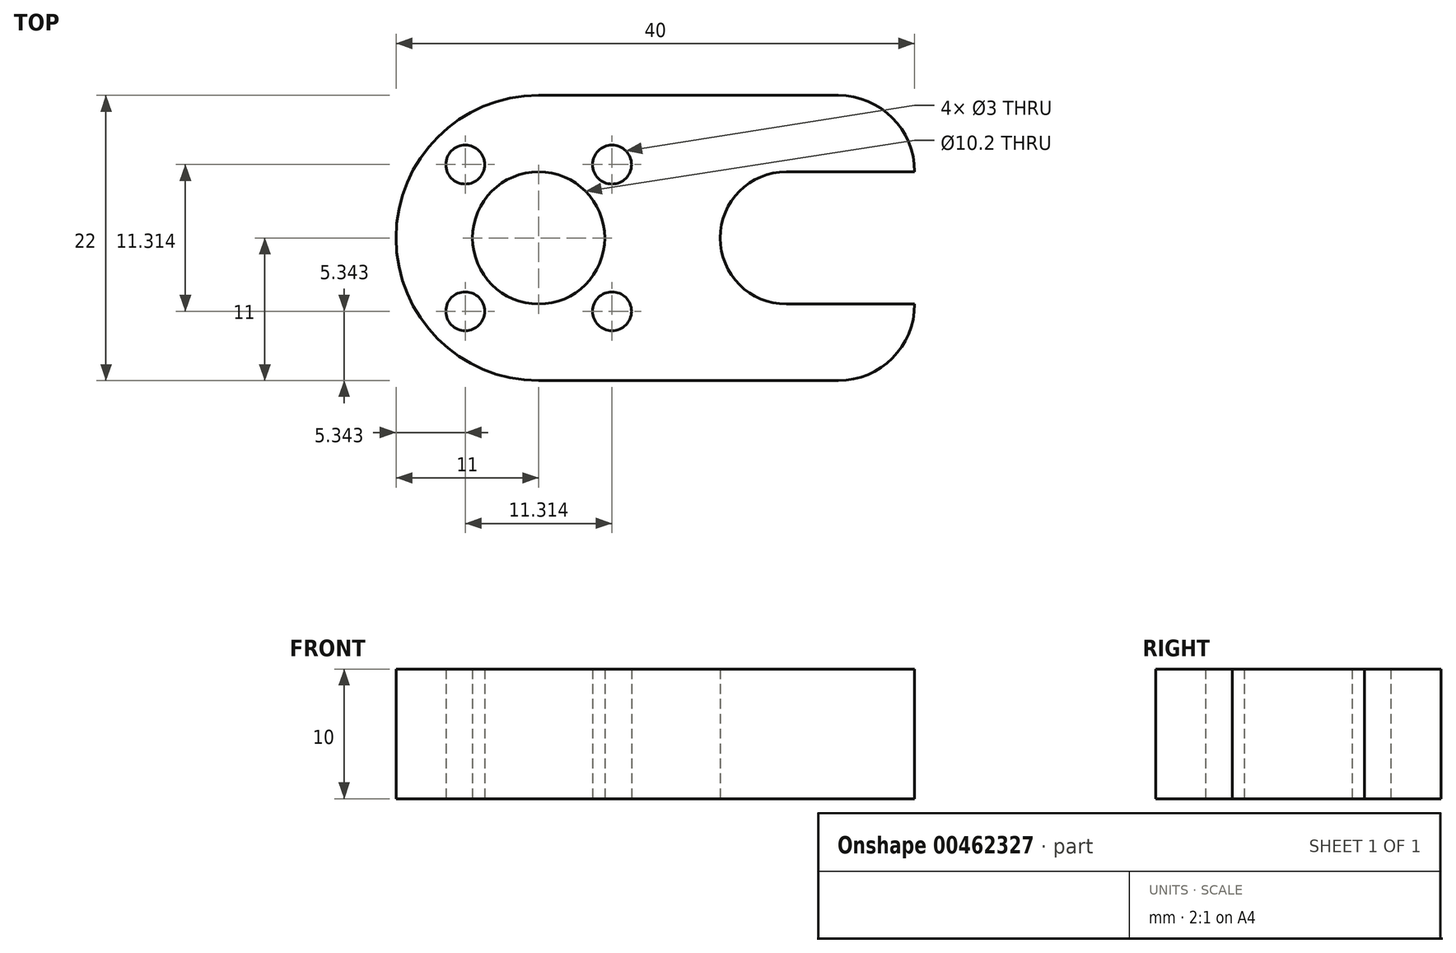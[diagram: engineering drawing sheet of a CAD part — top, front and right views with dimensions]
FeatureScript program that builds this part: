
annotation { "Feature Type Name" : "Feature", "Feature Type Description" : "" }
export const myFeature = defineFeature(function(context is Context, id is Id, definition is map)
    precondition{}
    {
        {
            var Q0;
            Q0=qCreatedBy(makeId("Top.planeOp"),FACE);
            var sketch = newSketch(context, id + "F0", { "sketchPlane" : qUnion([Q0])});
            skLineSegment(sketch, "E0.bottom", {"start": v(14.1, 11) * mm, "end": v(-9, 11) * mm});
            skLineSegment(sketch, "E0.top", {"start": v(14.1, -11) * mm, "end": v(-9, -11) * mm});
            skLineSegment(sketch, "E0.right", {"start": v(-20, 0) * mm, "end": v(-20, 0) * mm});
            skPoint(sketch, "E0.middle", {"position": v(0, 0) * mm});
            skPoint(sketch, "E1.visualSharp", {"position": v(-20, 11) * mm});
            skArc(sketch, "E1.filletArc", {"start": v(-9, 11) * mm, "mid": v(-16.78, 7.78) * mm, "end": v(-20, 0) * mm});
            skPoint(sketch, "E2.visualSharp", {"position": v(-20, -11) * mm});
            skArc(sketch, "E2.filletArc", {"start": v(-20, 0) * mm, "mid": v(-16.78, -7.78) * mm, "end": v(-9, -11) * mm});
            skPoint(sketch, "E3.visualSharp", {"position": v(20, 11) * mm});
            skArc(sketch, "E3.filletArc", {"start": v(20, 5.1) * mm, "mid": v(18.27, 9.27) * mm, "end": v(14.1, 11) * mm});
            skPoint(sketch, "E4.visualSharp", {"position": v(20, -11) * mm});
            skArc(sketch, "E4.filletArc", {"start": v(14.1, -11) * mm, "mid": v(18.27, -9.27) * mm, "end": v(20, -5.1) * mm});
            skLineSegment(sketch, "E5.bottom", {"start": v(20, 5.1) * mm, "end": v(10.1, 5.1) * mm});
            skLineSegment(sketch, "E5.top", {"start": v(20, -5.1) * mm, "end": v(10.1, -5.1) * mm});
            skLineSegment(sketch, "E5.right", {"start": v(5, 0) * mm, "end": v(5, 0) * mm});
            skPoint(sketch, "E6.visualSharp", {"position": v(5, 5.1) * mm});
            skArc(sketch, "E6.filletArc", {"start": v(10.1, 5.1) * mm, "mid": v(6.5, 3.6) * mm, "end": v(5, 0) * mm});
            skPoint(sketch, "E7.visualSharp", {"position": v(5, -5.1) * mm});
            skArc(sketch, "E7.filletArc", {"start": v(5, 0) * mm, "mid": v(6.5, -3.6) * mm, "end": v(10.1, -5.1) * mm});
            skCircle(sketch, "E8", {"center": v(-9, 0) * mm, "radius": 11 * mm, "construction": true});
            skLineSegment(sketch, "E9", {"start": v(-9, 11) * mm, "end": v(-9, -11) * mm, "construction": true});
            skLineSegment(sketch, "E10", {"start": v(-9, 0) * mm, "end": v(-1.22, -7.78) * mm, "construction": true});
            skCircle(sketch, "E11", {"center": v(-3.34, -5.66) * mm, "radius": 1.5 * mm});
            skCircle(sketch, "E12", {"center": v(-9, 0) * mm, "radius": 5.1 * mm});
            skCircle(sketch, "E13.MirrorC", {"center": v(-14.66, -5.66) * mm, "radius": 1.5 * mm});
            skCircle(sketch, "E14.MirrorC", {"center": v(-14.66, 5.66) * mm, "radius": 1.5 * mm});
            skCircle(sketch, "E15.MirrorC", {"center": v(-3.34, 5.66) * mm, "radius": 1.5 * mm});
            skSolve(sketch);
        }
        {
            var Q0;
            Q0 = qSketchRegion(id + "F0", true);
            extrude(context, id + "F1", {"entities" : qUnion([Q0]), "depth" : 10 * mm});
        }
    });
